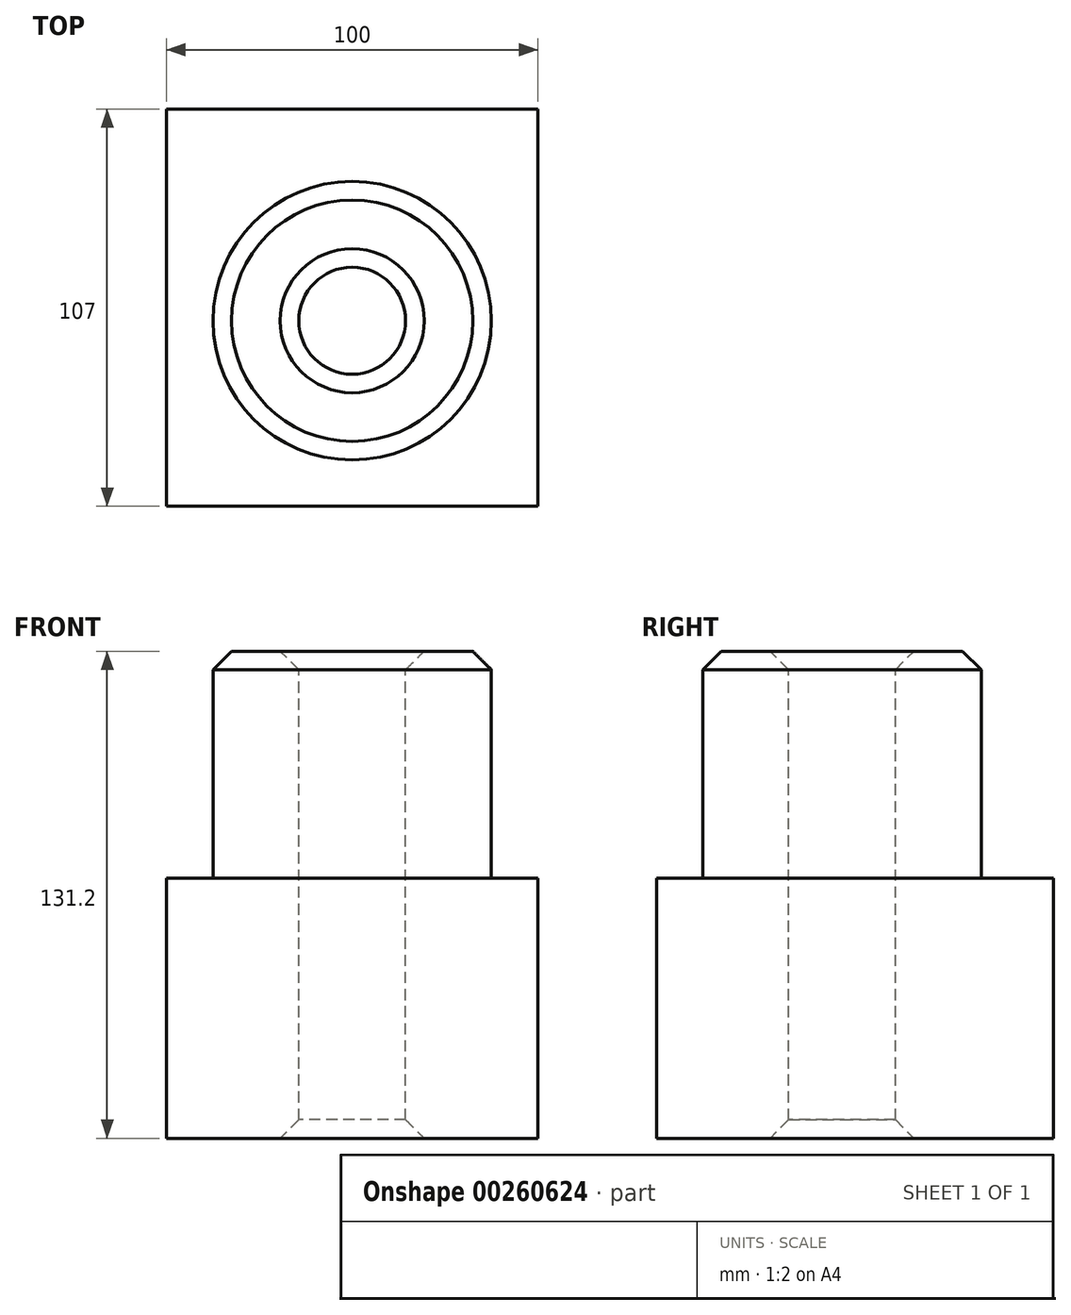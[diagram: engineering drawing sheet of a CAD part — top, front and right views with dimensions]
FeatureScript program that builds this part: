
annotation { "Feature Type Name" : "Feature", "Feature Type Description" : "" }
export const myFeature = defineFeature(function(context is Context, id is Id, definition is map)
    precondition{}
    {
        {
            var Q0;
            Q0=qCreatedBy(makeId("Front.planeOp"),FACE);
            var sketch = newSketch(context, id + "F0", { "sketchPlane" : qUnion([Q0])});
            skLineSegment(sketch, "E0.bottom", {"start": v(0, 0) * mm, "end": v(100, 0) * mm});
            skLineSegment(sketch, "E0.top", {"start": v(0, 70) * mm, "end": v(100, 70) * mm});
            skLineSegment(sketch, "E0.left", {"start": v(0, 0) * mm, "end": v(0, 70) * mm});
            skLineSegment(sketch, "E0.right", {"start": v(100, 0) * mm, "end": v(100, 70) * mm});
            skSolve(sketch);
        }
        {
            var Q0;
            Q0=qSketchRegion(id+"F0",true);
            extrude(context, id + "F1", {"entities" : qUnion([Q0]), "depth" : 107 * mm});
        }
        {
            var Q0;
            Q0=makeQuery(id+"F1.opExtrude","SWEPT_FACE",FACE,{"disambiguationData":[OSD([sQuery(id+"F0.wireOp",EDGE,"E0.top")])]});
            var sketch = newSketch(context, id + "F2", { "sketchPlane" : qUnion([Q0])});
            skCircle(sketch, "E1", {"center": v(50, -57) * mm, "radius": 37.5 * mm});
            skSolve(sketch);
        }
        {
            var Q0;
            Q0=qSketchRegion(id+"F2",true);
            extrude(context, id + "F3", {"entities" : qUnion([Q0]), "operationType" : NewBodyOperationType.ADD, "depth" : 61.2 * mm});
        }
        {
            var Q0;
            Q0=makeQuery(id+"F3.opExtrude","CAP_FACE",FACE,{"disambiguationData":[OSD([sQuery(id+"F2.wireOp",EDGE,"E1")])],"isStart":false});
            var sketch = newSketch(context, id + "F4", { "sketchPlane" : qUnion([Q0])});
            skCircle(sketch, "E2.0", {"center": v(50, -57) * mm, "radius": 14.4 * mm});
            skSolve(sketch);
        }
        {
            var Q0;
            Q0=makeQuery(id+"F4.imprint","IMPRINT",FACE,{"disambiguationData":[TD([[makeQuery(id+"F4.imprint","IMPRINT",EDGE,{"derivedFrom":sQuery(id+"F4.wireOp",EDGE,"E2.0")}),1.0]])]});
            extrude(context, id + "F5", {"entities" : qUnion([Q0]), "operationType" : NewBodyOperationType.REMOVE, "endBound" : BoundingType.THROUGH_ALL, "oppositeDirection" : true, "depth" : 25 * mm});
        }
        {
            var Q0;
            Q0=makeQuery(id+"F3.opExtrude","CAP_FACE",FACE,{"disambiguationData":[OSD([sQuery(id+"F2.wireOp",EDGE,"E1")])],"isStart":false});
            var Q1;
            Q1=makeQuery(id+"F5.boolean.opBoolean","INTERSECT",EDGE,{"derivedFrom":[makeQuery(id+"F1.opExtrude","SWEPT_FACE",FACE,{"disambiguationData":[OSD([sQuery(id+"F0.wireOp",EDGE,"E0.bottom")])]}),makeQuery(id+"F5.opExtrude","SWEPT_FACE",FACE,{"disambiguationData":[OSD([sQuery(id+"F4.wireOp",EDGE,"E2.0")])]})]});
            chamfer(context, id + "F6", {"entities" : qUnion([Q0, Q1]), "width" : 5 * mm, "tangentPropagation" : true});
        }
    });
